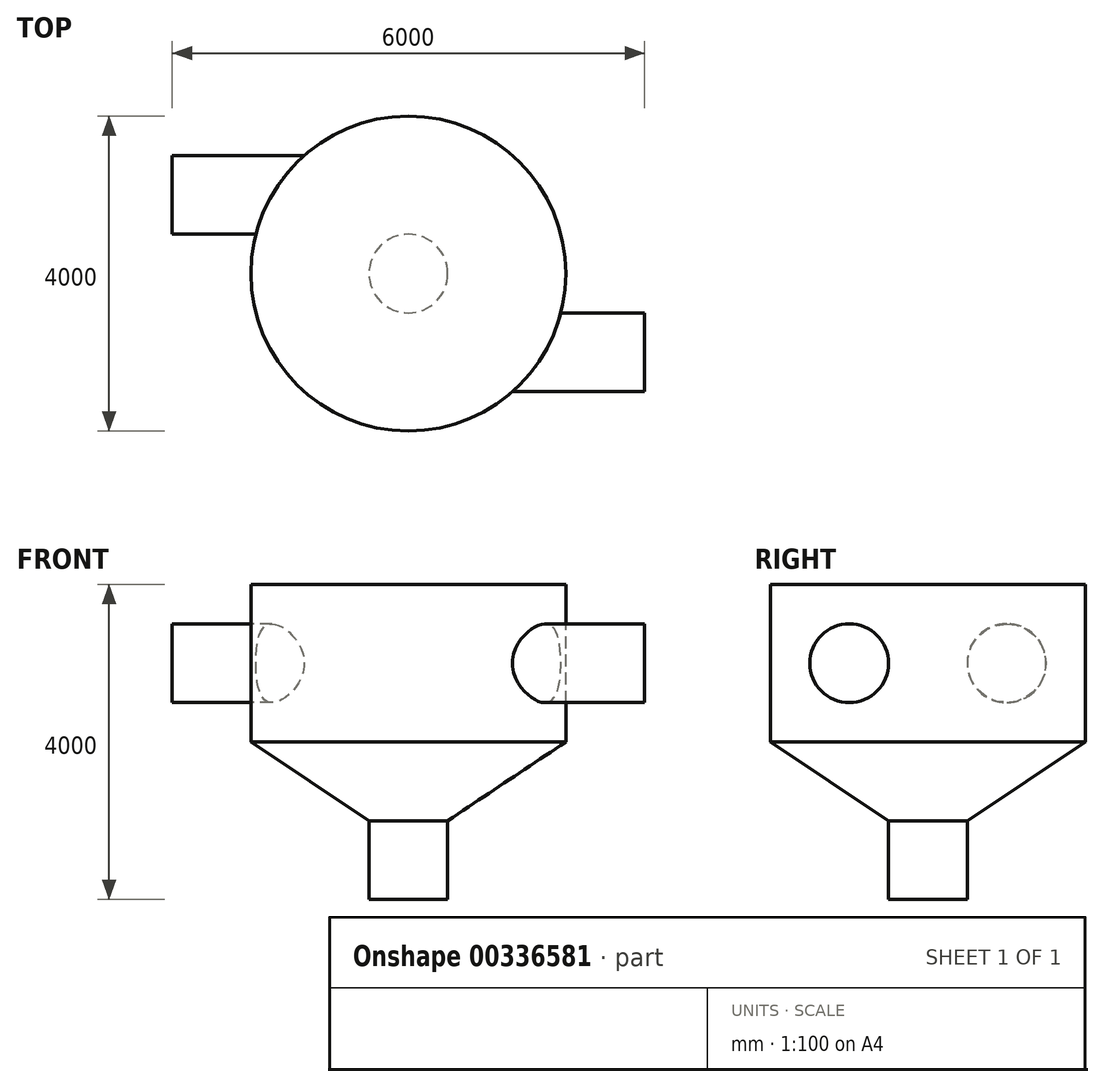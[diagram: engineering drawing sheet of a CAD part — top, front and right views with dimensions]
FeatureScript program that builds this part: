
annotation { "Feature Type Name" : "Feature", "Feature Type Description" : "" }
export const myFeature = defineFeature(function(context is Context, id is Id, definition is map)
    precondition{}
    {
        {
            var Q0;
            Q0=qCreatedBy(makeId("Front.planeOp"),FACE);
            var sketch = newSketch(context, id + "F0", { "sketchPlane" : qUnion([Q0])});
            skLineSegment(sketch, "E0", {"start": v(0, 0) * mm, "end": v(500, 0) * mm});
            skLineSegment(sketch, "E1", {"start": v(500, 0) * mm, "end": v(500, 1000) * mm});
            skLineSegment(sketch, "E2", {"start": v(0, 0) * mm, "end": v(2000, 0) * mm, "construction": true});
            skLineSegment(sketch, "E3", {"start": v(2000, 0) * mm, "end": v(2000, 2000) * mm, "construction": true});
            skLineSegment(sketch, "E4", {"start": v(500, 1000) * mm, "end": v(2000, 2000) * mm});
            skLineSegment(sketch, "E5", {"start": v(2000, 2000) * mm, "end": v(2000, 4000) * mm});
            skLineSegment(sketch, "E6", {"start": v(2000, 4000) * mm, "end": v(0, 4000) * mm});
            skLineSegment(sketch, "E7", {"start": v(0, 4000) * mm, "end": v(0, 0) * mm});
            skSolve(sketch);
        }
        {
            var Q0;
            Q0 = qSketchRegion(id + "F0", true);
            var Q1;
            Q1=sQuery(id+"F0.wireOp",EDGE,"E7");
            revolve(context, id + "F1", {"entities" : qUnion([Q0]), "axis" : qUnion([Q1]), "revolveType" : RevolveType.FULL});
        }
        {
            var Q0;
            Q0=qCreatedBy(makeId("Right.planeOp"),FACE);
            cPlane(context, id + "F2", {"entities" : qUnion([Q0]), "cplaneType" : CPlaneType.OFFSET, "offset" : 3000 * mm, "oppositeDirection" : true, "width" : 150 * mm, "height" : 150 * mm});
        }
        {
            var Q0;
            Q0=qCreatedBy(id+"F2.planeOp",FACE);
            var sketch = newSketch(context, id + "F3", { "sketchPlane" : qUnion([Q0])});
            skLineSegment(sketch, "E8", {"start": v(0, 0) * mm, "end": v(1000, 0) * mm, "construction": true});
            skLineSegment(sketch, "E9", {"start": v(1000, 0) * mm, "end": v(1000, 3000) * mm, "construction": true});
            skCircle(sketch, "E10", {"center": v(1000, 3000) * mm, "radius": 500 * mm});
            skSolve(sketch);
        }
        {
            var Q0;
            Q0=qCreatedBy(makeId("Right.planeOp"),FACE);
            cPlane(context, id + "F4", {"entities" : qUnion([Q0]), "cplaneType" : CPlaneType.OFFSET, "offset" : 3000 * mm, "width" : 150 * mm, "height" : 150 * mm});
        }
        {
            var Q0;
            Q0=qCreatedBy(id+"F4.planeOp",FACE);
            var sketch = newSketch(context, id + "F5", { "sketchPlane" : qUnion([Q0])});
            skLineSegment(sketch, "E11", {"start": v(0, 0) * mm, "end": v(-1000, 0) * mm, "construction": true});
            skLineSegment(sketch, "E12", {"start": v(-1000, 0) * mm, "end": v(-1000, 3000) * mm, "construction": true});
            skCircle(sketch, "E13", {"center": v(-1000, 3000) * mm, "radius": 500 * mm});
            skSolve(sketch);
        }
        {
            var Q0;
            Q0 = qSketchRegion(id + "F3", true);
            extrude(context, id + "F6", {"entities" : qUnion([Q0]), "operationType" : NewBodyOperationType.ADD, "endBound" : BoundingType.UP_TO_NEXT, "depth" : 25 * mm});
        }
        {
            var Q0;
            Q0 = qSketchRegion(id + "F5", true);
            extrude(context, id + "F7", {"entities" : qUnion([Q0]), "endBound" : BoundingType.UP_TO_NEXT, "oppositeDirection" : true, "depth" : 25 * mm});
        }
    });
